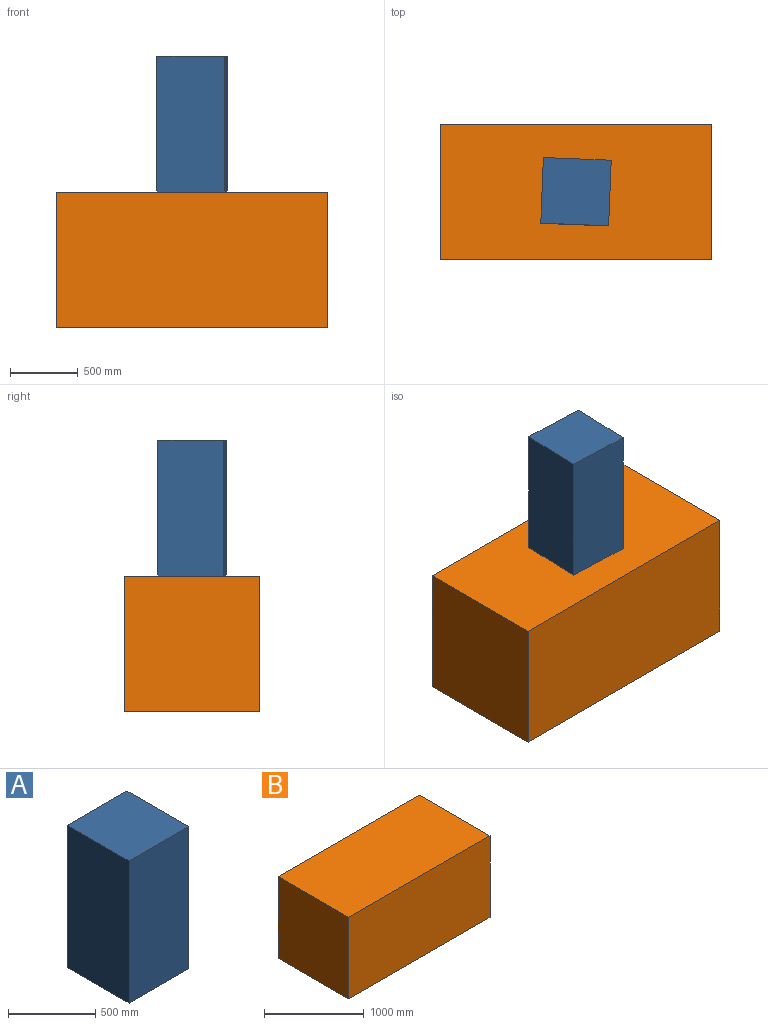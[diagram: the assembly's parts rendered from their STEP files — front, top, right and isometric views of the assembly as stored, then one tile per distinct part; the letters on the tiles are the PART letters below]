
ASSEMBLY  parts=2 mates=1
PART A: 6 faces, bbox 483.3x500x1000 mm
  f0: plane 1000x483.33mm, normal (0,1,0), area 483333.3mm2, adj f1,f3,f4,f5
  f1: plane 1000x500mm, normal (-1,0,0), area 500000mm2, adj f0,f2,f4,f5
  f2: plane 1000x483.33mm, normal (0,-1,0), area 483333.3mm2, adj f1,f3,f4,f5
  f3: plane 1000x500mm, normal (1,0,0), area 500000mm2, adj f0,f2,f4,f5
  f4: plane 500x483.33mm, normal (0,0,1), area 241666.7mm2, adj f0,f1,f2,f3
  f5: plane 500x483.33mm, normal (0,0,-1), area 241666.7mm2, adj f0,f1,f2,f3
PART B: 6 faces, bbox 2000x1000x1000 mm
  f0: plane 1000x1000mm, normal (-1,0,0), area 1000000mm2, adj f1,f3,f4,f5
  f1: plane 2000x1000mm, normal (0,-1,0), area 2000000mm2, adj f0,f2,f4,f5
  f2: plane 1000x1000mm, normal (1,0,0), area 1000000mm2, adj f1,f3,f4,f5
  f3: plane 2000x1000mm, normal (0,1,0), area 2000000mm2, adj f0,f2,f4,f5
  f4: plane 2000x1000mm, normal (0,0,1), area 2000000mm2, adj f0,f1,f2,f3
  f5: plane 2000x1000mm, normal (0,0,-1), area 2000000mm2, adj f0,f1,f2,f3
PLACE A rot(axis=(0,0,-1),92.3deg) t=(1000,500,1500)mm
PLACE B at identity fixed
MATE revolute B.f4 <-> A.f5  axis (0,0,1) through (1000,500,1000)mm
